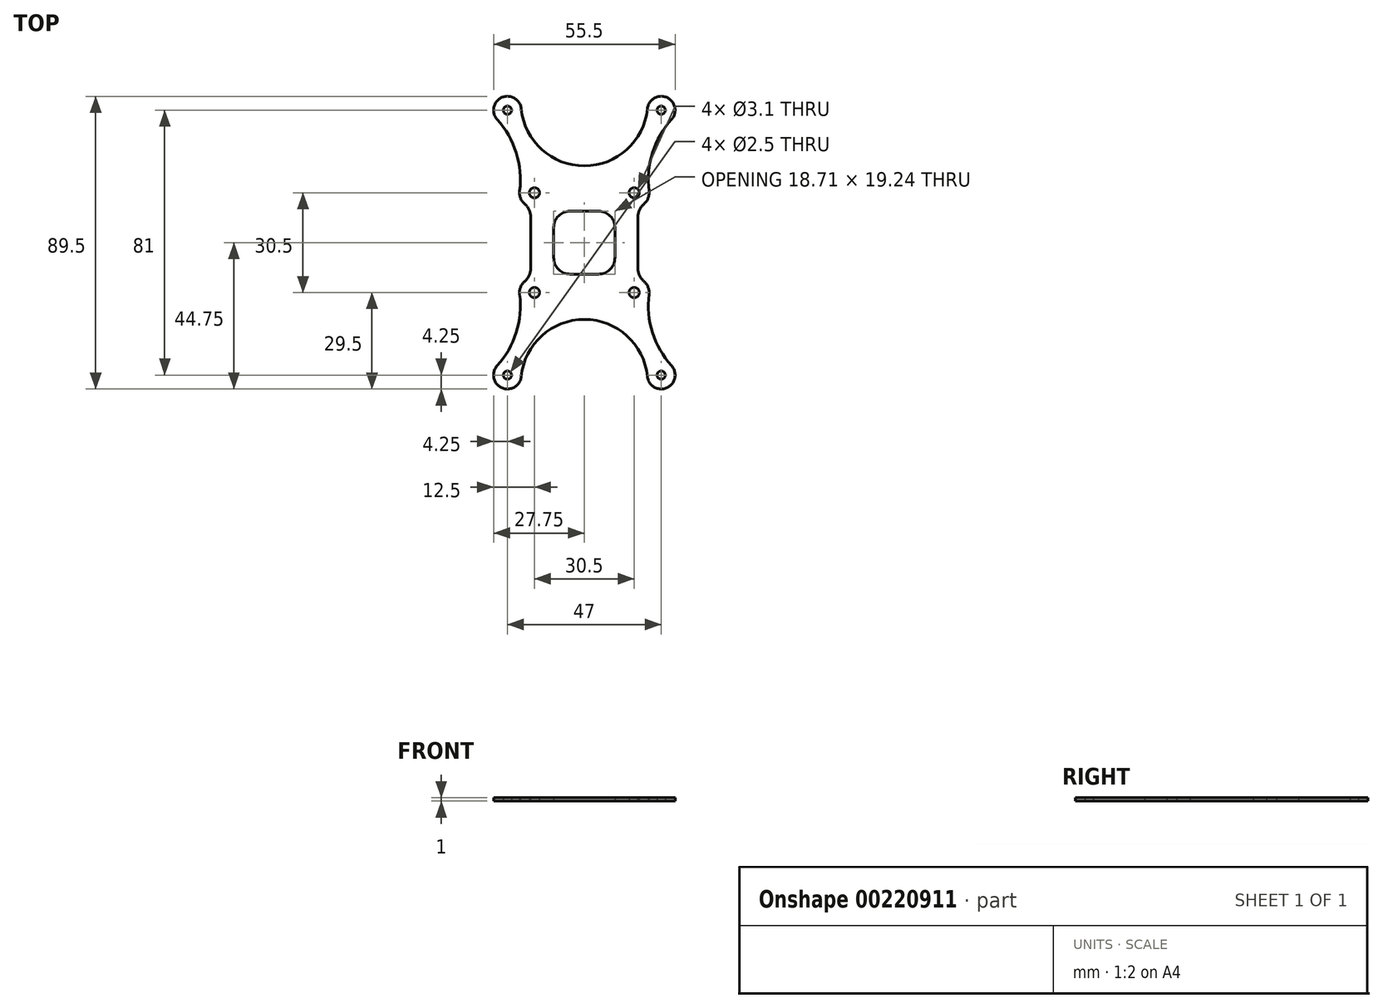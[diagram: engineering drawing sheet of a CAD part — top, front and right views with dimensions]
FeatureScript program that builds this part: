
annotation { "Feature Type Name" : "Feature", "Feature Type Description" : "" }
export const myFeature = defineFeature(function(context is Context, id is Id, definition is map)
    precondition{}
    {
        {
            var Q0;
            Q0=qCreatedBy(makeId("Top.planeOp"),FACE);
            var sketch = newSketch(context, id + "F0", { "sketchPlane" : qUnion([Q0])});
            skCircle(sketch, "E0", {"center": v(-23.5, 40.5) * mm, "radius": 1.25 * mm});
            skLineSegment(sketch, "E1.bottom", {"start": v(-23.5, 40.5) * mm, "end": v(23.5, 40.5) * mm, "construction": true});
            skLineSegment(sketch, "E1.top", {"start": v(-23.5, -40.5) * mm, "end": v(23.5, -40.5) * mm, "construction": true});
            skLineSegment(sketch, "E1.left", {"start": v(-23.5, 40.5) * mm, "end": v(-23.5, -40.5) * mm, "construction": true});
            skLineSegment(sketch, "E1.right", {"start": v(23.5, 40.5) * mm, "end": v(23.5, -40.5) * mm, "construction": true});
            skCircle(sketch, "E2", {"center": v(-15.25, 15.25) * mm, "radius": 1.55 * mm});
            skArc(sketch, "E3.0", {"start": v(-19.25, 40.5) * mm, "mid": v(-25.03, 44.47) * mm, "end": v(-26.65, 37.65) * mm});
            skArc(sketch, "E4.0", {"start": v(-16.4, 10.85) * mm, "mid": v(-19.02, 12.7) * mm, "end": v(-19.76, 15.81) * mm});
            skLineSegment(sketch, "E5.bottom", {"start": v(-15.25, 15.25) * mm, "end": v(0, 15.2) * mm, "construction": true});
            skLineSegment(sketch, "E5.left", {"start": v(-15.25, 15.25) * mm, "end": v(-15.3, 0) * mm, "construction": true});
            skArc(sketch, "E6", {"start": v(-19.76, 15.81) * mm, "mid": v(-20.83, 27.48) * mm, "end": v(-26.65, 37.65) * mm});
            skLineSegment(sketch, "E7", {"start": v(-16.4, 10.85) * mm, "end": v(-16.4, 0) * mm});
            skCircle(sketch, "E8", {"center": v(23.5, 40.5) * mm, "radius": 4.25 * mm, "construction": true});
            skArc(sketch, "E9", {"start": v(-19.27, 40.92) * mm, "mid": v(-13, 28.47) * mm, "end": v(0, 23.46) * mm});
            skPoint(sketch, "E10", {"position": v(0, 40.5) * mm});
            skLineSegment(sketch, "E11", {"start": v(0, 23.46) * mm, "end": v(0, 9.62) * mm});
            skLineSegment(sketch, "E12", {"start": v(-16.4, 0) * mm, "end": v(-9.35, 0) * mm});
            skArc(sketch, "E13.trimOffspring", {"start": v(19.22, 40.5) * mm, "mid": v(19.25, 40.7) * mm, "end": v(19.27, 40.92) * mm});
            skLineSegment(sketch, "E14.top", {"start": v(0, 9.62) * mm, "end": v(-9.35, 9.62) * mm});
            skLineSegment(sketch, "E14.right", {"start": v(-9.35, 0) * mm, "end": v(-9.35, 9.62) * mm});
            skSolve(sketch);
        }
        {
            var Q0;
            Q0 = qSketchRegion(id + "F0", true);
            extrude(context, id + "F1", {"entities" : qUnion([Q0]), "depth" : 1 * mm});
        }
        {
            var Q0;
            Q0=makeQuery(id+"F4.opPattern","COPY",EDGE,{"derivedFrom":makeQuery(id+"F3.opPattern","COPY",EDGE,{"derivedFrom":makeQuery(id+"F1.opExtrude","SWEPT_EDGE",EDGE,{"disambiguationData":[OSD([sQuery(id+"F0.wireOp",EDGE,"E14.top"),sQuery(id+"F0.wireOp",EDGE,"E14.right")])]}),"instanceName":"1"}),"instanceName":"1"});
            var Q1;
            Q1=makeQuery(id+"F1.opExtrude","SWEPT_EDGE",EDGE,{"disambiguationData":[OSD([sQuery(id+"F0.wireOp",EDGE,"E14.top"),sQuery(id+"F0.wireOp",EDGE,"E14.right")])]});
            var Q2;
            Q2=makeQuery(id+"F1.opExtrude","SWEPT_EDGE",EDGE,{"disambiguationData":[OSD([sQuery(id+"F0.wireOp",EDGE,"E4.0"),sQuery(id+"F0.wireOp",EDGE,"E7")])]});
            fillet(context, id + "F2", {"entities" : qUnion([Q0, Q1, Q2]), "radius" : 5 * mm, "tangentPropagation" : true, "allowEdgeOverflow" : false});
        }
        {
            var Q0;
            Q0=makeQuery(id+"F1.opExtrude","SWEPT_BODY",BODY,{"disambiguationData":[OSD([sQuery(id+"F0.wireOp",EDGE,"E0"),sQuery(id+"F0.wireOp",EDGE,"E2"),sQuery(id+"F0.wireOp",EDGE,"E3.0"),sQuery(id+"F0.wireOp",EDGE,"E4.0"),sQuery(id+"F0.wireOp",EDGE,"E6"),sQuery(id+"F0.wireOp",EDGE,"E7"),sQuery(id+"F0.wireOp",EDGE,"E9"),sQuery(id+"F0.wireOp",EDGE,"E11"),sQuery(id+"F0.wireOp",EDGE,"E12"),sQuery(id+"F0.wireOp",EDGE,"E14.top"),sQuery(id+"F0.wireOp",EDGE,"E14.right")])]});
            var Q1;
            Q1=makeQuery(id+"F1.opExtrude","SWEPT_FACE",FACE,{"disambiguationData":[OSD([sQuery(id+"F0.wireOp",EDGE,"E12")])]});
            mirror(context, id + "F3", {"operationType" : NewBodyOperationType.ADD, "entities" : qUnion([Q0]), "mirrorPlane" : qUnion([Q1])});
        }
        {
            var Q0;
            Q0=makeQuery(id+"F1.opExtrude","SWEPT_BODY",BODY,{"disambiguationData":[OSD([sQuery(id+"F0.wireOp",EDGE,"E0"),sQuery(id+"F0.wireOp",EDGE,"E2"),sQuery(id+"F0.wireOp",EDGE,"E3.0"),sQuery(id+"F0.wireOp",EDGE,"E4.0"),sQuery(id+"F0.wireOp",EDGE,"E6"),sQuery(id+"F0.wireOp",EDGE,"E7"),sQuery(id+"F0.wireOp",EDGE,"E9"),sQuery(id+"F0.wireOp",EDGE,"E11"),sQuery(id+"F0.wireOp",EDGE,"E12"),sQuery(id+"F0.wireOp",EDGE,"E14.top"),sQuery(id+"F0.wireOp",EDGE,"E14.right")])]});
            var Q1;
            Q1=makeQuery(id+"F1.opExtrude","SWEPT_FACE",FACE,{"disambiguationData":[OSD([sQuery(id+"F0.wireOp",EDGE,"E11")])]});
            mirror(context, id + "F4", {"operationType" : NewBodyOperationType.ADD, "entities" : qUnion([Q0]), "mirrorPlane" : qUnion([Q1])});
        }
    });
